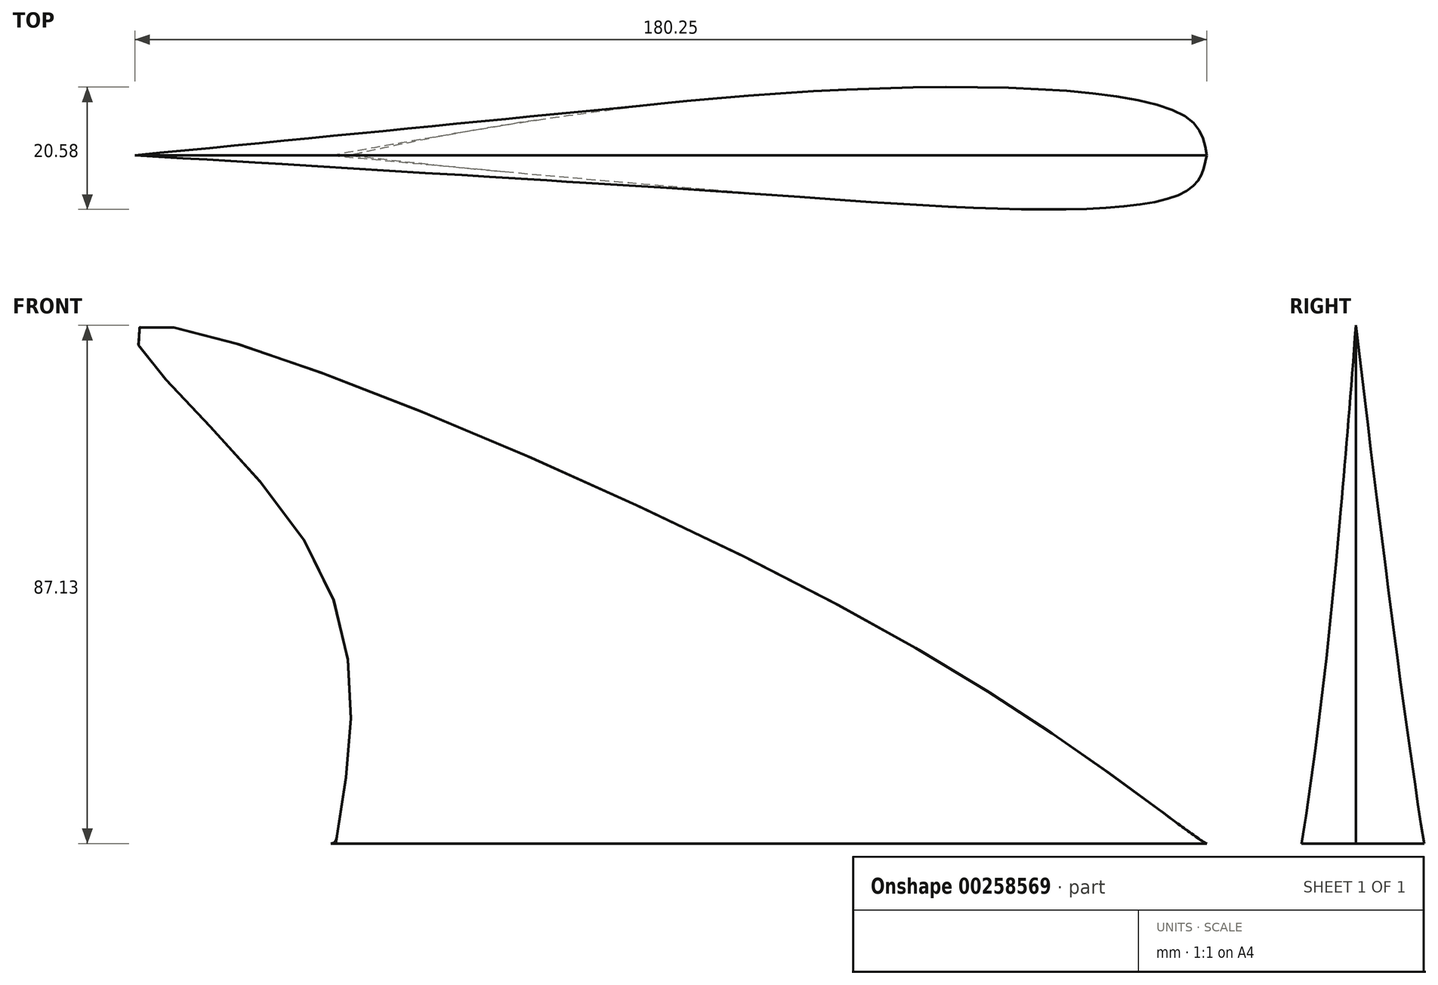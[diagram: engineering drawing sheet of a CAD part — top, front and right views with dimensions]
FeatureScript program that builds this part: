
annotation { "Feature Type Name" : "Feature", "Feature Type Description" : "" }
export const myFeature = defineFeature(function(context is Context, id is Id, definition is map)
    precondition{}
    {
        {
            var Q0;
            Q0=qCreatedBy(makeId("Top.planeOp"),FACE);
            var sketch = newSketch(context, id + "F0", { "sketchPlane" : qUnion([Q0])});
            skFitSpline(sketch, "E0", {"points": [v(-74.68, 0) * mm, v(0, 10.37) * mm, v(68.88, 6.64) * mm, v(72.6, 0) * mm], "startDerivative": vector(157.1, 28.65) * mm, "endDerivative": vector(8.1, -51.72) * mm});
            skFitSpline(sketch, "E1", {"points": [v(-74.68, 0) * mm, v(0, -6.64) * mm, v(68.88, -6.22) * mm, v(72.6, 0) * mm], "startDerivative": vector(156.88, -14.87) * mm, "endDerivative": vector(9.11, 50.87) * mm});
            skSolve(sketch);
        }
        {
            var Q0;
            Q0=qCreatedBy(makeId("Front.planeOp"),FACE);
            var sketch = newSketch(context, id + "F1", { "sketchPlane" : qUnion([Q0])});
            skFitSpline(sketch, "E2", {"points": [v(72.2, 0) * mm, v(0, 45.64) * mm, v(-107.46, 86.3) * mm, v(-78.42, 49.79) * mm, v(-73.85, 0) * mm], "startDerivative": vector(-203.82, 153.05) * mm, "endDerivative": vector(-39.55, -236.84) * mm});
            skSolve(sketch);
        }
        {
            var Q0;
            Q0=sQuery(id+"F1.wireOp",EDGE,"E2");
            var Q1;
            Q1=sQuery(id+"F0.wireOp",EDGE,"E0");
            loft(context, id + "F2", {"bodyType" : ToolBodyType.SURFACE, "wireProfilesArray" : [{ "wireProfileEntities" : qUnion([Q0]) }, { "wireProfileEntities" : qUnion([Q1]) }]});
        }
        {
            var Q0;
            Q0=sQuery(id+"F0.wireOp",EDGE,"E1");
            var Q1;
            Q1=sQuery(id+"F1.wireOp",EDGE,"E2");
            loft(context, id + "F3", {"bodyType" : ToolBodyType.SURFACE, "wireProfilesArray" : [{ "wireProfileEntities" : qUnion([Q0]) }, { "wireProfileEntities" : qUnion([Q1]) }]});
        }
    });
